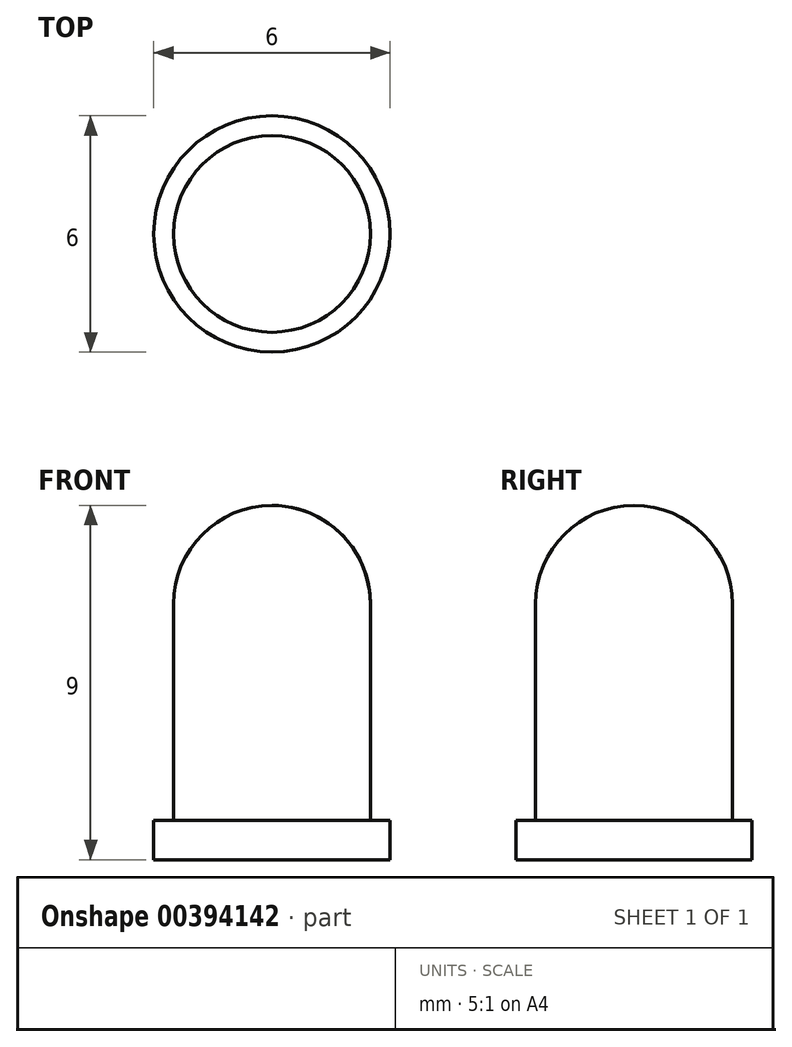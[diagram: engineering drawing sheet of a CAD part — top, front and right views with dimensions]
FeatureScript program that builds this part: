
annotation { "Feature Type Name" : "Feature", "Feature Type Description" : "" }
export const myFeature = defineFeature(function(context is Context, id is Id, definition is map)
    precondition{}
    {
        {
            var Q0;
            Q0=qCreatedBy(makeId("Top.planeOp"),FACE);
            var sketch = newSketch(context, id + "F0", { "sketchPlane" : qUnion([Q0])});
            skCircle(sketch, "E0", {"center": v(0, 0) * mm, "radius": 3 * mm});
            skSolve(sketch);
        }
        {
            var Q0;
            Q0 = qSketchRegion(id + "F0", true);
            extrude(context, id + "F1", {"entities" : qUnion([Q0]), "depth" : 1 * mm});
        }
        {
            var Q0;
            Q0=makeQuery(id+"F1.opExtrude","CAP_FACE",FACE,{"disambiguationData":[OSD([sQuery(id+"F0.wireOp",EDGE,"E0")])],"isStart":false});
            var sketch = newSketch(context, id + "F2", { "sketchPlane" : qUnion([Q0])});
            skCircle(sketch, "E1", {"center": v(0, 0) * mm, "radius": 2.5 * mm});
            skSolve(sketch);
        }
        {
            var Q0;
            Q0=makeQuery(id+"F2.imprint","IMPRINT",FACE,{"disambiguationData":[TD([[makeQuery(id+"F2.imprint","IMPRINT",EDGE,{"derivedFrom":sQuery(id+"F2.wireOp",EDGE,"E1")}),1.0]])]});
            extrude(context, id + "F3", {"entities" : qUnion([Q0]), "operationType" : NewBodyOperationType.ADD, "depth" : 8 * mm});
        }
        {
            var Q0;
            Q0=makeQuery(id+"F3.opExtrude","CAP_EDGE",EDGE,{"disambiguationData":[OSD([sQuery(id+"F2.wireOp",EDGE,"E1")])],"isStart":false});
            fillet(context, id + "F4", {"entities" : qUnion([Q0]), "radius" : 2.5 * mm, "tangentPropagation" : true, "allowEdgeOverflow" : false});
        }
    });
